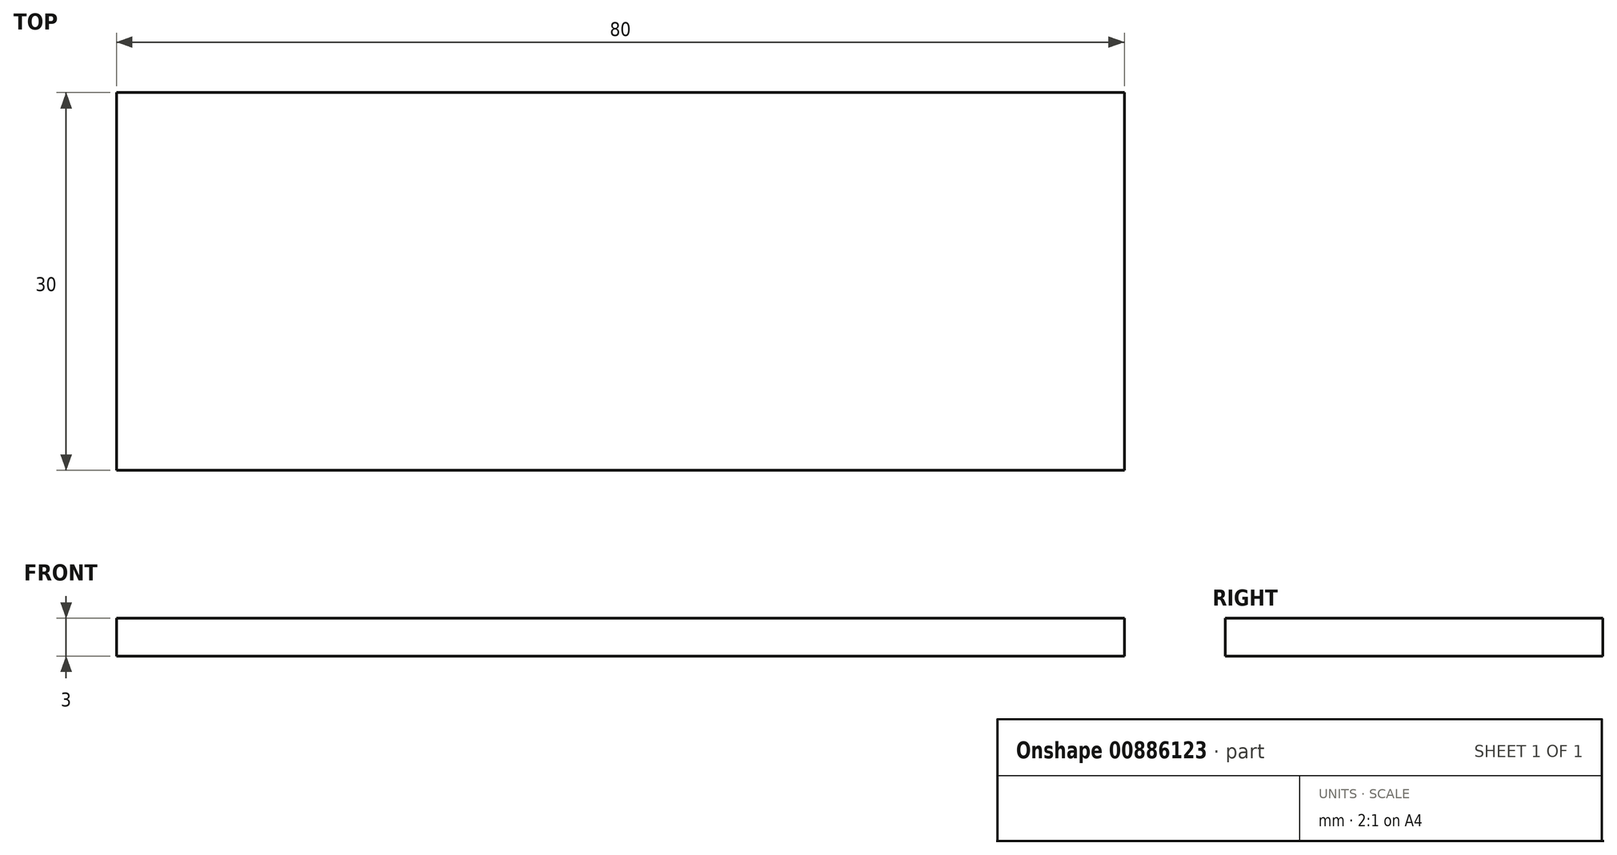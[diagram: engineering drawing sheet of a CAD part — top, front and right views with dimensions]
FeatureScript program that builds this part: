
annotation { "Feature Type Name" : "Feature", "Feature Type Description" : "" }
export const myFeature = defineFeature(function(context is Context, id is Id, definition is map)
    precondition{}
    {
        {
            var Q0;
            Q0=qCreatedBy(makeId("Top.planeOp"),FACE);
            var sketch = newSketch(context, id + "F0", { "sketchPlane" : qUnion([Q0])});
            skLineSegment(sketch, "E0.bottom", {"start": v(-38.84, 9.92) * mm, "end": v(41.16, 9.92) * mm});
            skLineSegment(sketch, "E0.top", {"start": v(-38.84, -20.08) * mm, "end": v(41.16, -20.08) * mm});
            skLineSegment(sketch, "E0.left", {"start": v(-38.84, 9.92) * mm, "end": v(-38.84, -20.08) * mm});
            skLineSegment(sketch, "E0.right", {"start": v(41.16, 9.92) * mm, "end": v(41.16, -20.08) * mm});
            skSolve(sketch);
        }
        {
            var Q0;
            Q0 = qSketchRegion(id + "F0", true);
            extrude(context, id + "F1", {"entities" : qUnion([Q0]), "depth" : 3 * mm, "offsetDistance" : 25 * mm});
        }
    });
